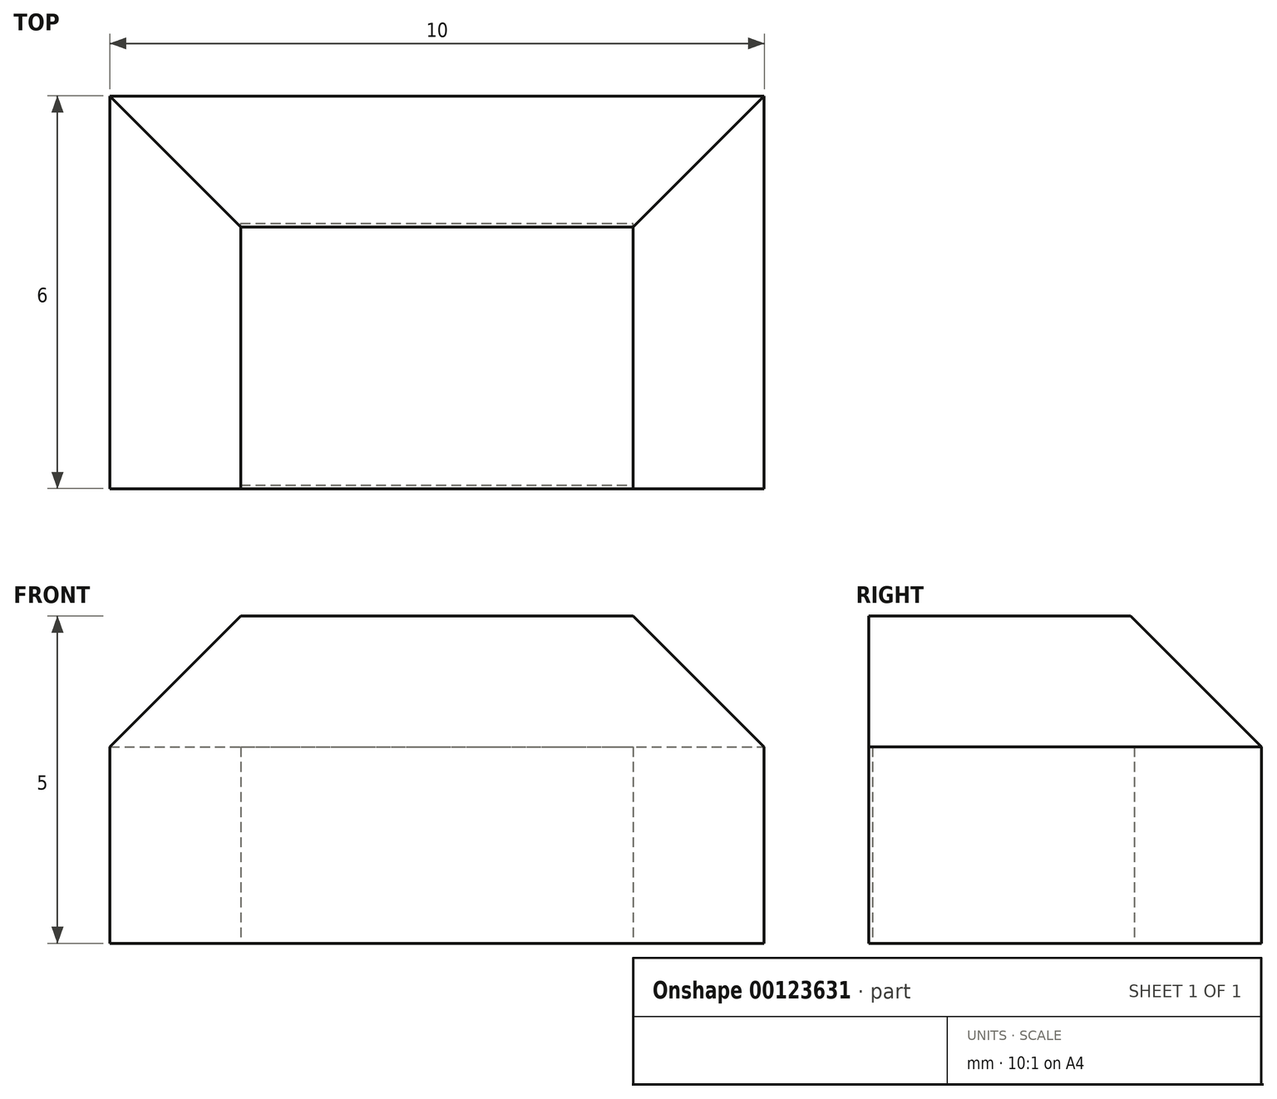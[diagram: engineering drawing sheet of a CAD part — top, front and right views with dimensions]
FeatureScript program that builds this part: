
annotation { "Feature Type Name" : "Feature", "Feature Type Description" : "" }
export const myFeature = defineFeature(function(context is Context, id is Id, definition is map)
    precondition{}
    {
        {
            var Q0;
            Q0=qCreatedBy(makeId("Top.planeOp"),FACE);
            var sketch = newSketch(context, id + "F0", { "sketchPlane" : qUnion([Q0])});
            skLineSegment(sketch, "E0.bottom", {"start": v(-27.54, 18.57) * mm, "end": v(-17.54, 18.57) * mm});
            skLineSegment(sketch, "E0.top", {"start": v(-27.54, 12.57) * mm, "end": v(-17.54, 12.57) * mm});
            skLineSegment(sketch, "E0.left", {"start": v(-27.54, 18.57) * mm, "end": v(-27.54, 12.57) * mm});
            skLineSegment(sketch, "E0.right", {"start": v(-17.54, 18.57) * mm, "end": v(-17.54, 12.57) * mm});
            skSolve(sketch);
        }
        {
            var Q0;
            Q0=makeQuery(id+"F0.imprint","IMPRINT",FACE,{"disambiguationData":[TD([[makeQuery(id+"F0.imprint","IMPRINT",EDGE,{"derivedFrom":sQuery(id+"F0.wireOp",EDGE,"E0.bottom")}),-1.0]])]});
            var sketch = newSketch(context, id + "F1", { "sketchPlane" : qUnion([Q0])});
            skLineSegment(sketch, "E1.bottom", {"start": v(-25.54, 12.62) * mm, "end": v(-19.54, 12.62) * mm});
            skLineSegment(sketch, "E1.top", {"start": v(-25.54, 16.62) * mm, "end": v(-19.54, 16.62) * mm});
            skLineSegment(sketch, "E1.left", {"start": v(-25.54, 12.62) * mm, "end": v(-25.54, 16.62) * mm});
            skLineSegment(sketch, "E1.right", {"start": v(-19.54, 12.62) * mm, "end": v(-19.54, 16.62) * mm});
            skSolve(sketch);
        }
        {
            var Q0;
            Q0=makeQuery(id+"F0.imprint","IMPRINT",FACE,{"disambiguationData":[TD([[makeQuery(id+"F0.imprint","IMPRINT",EDGE,{"derivedFrom":sQuery(id+"F0.wireOp",EDGE,"E0.bottom")}),-1.0]])]});
            extrude(context, id + "F2", {"entities" : qUnion([Q0]), "depth" : 5 * mm});
        }
        {
            var Q0;
            Q0=makeQuery(id+"F1.imprint","IMPRINT",FACE,{"disambiguationData":[TD([[makeQuery(id+"F1.imprint","IMPRINT",EDGE,{"derivedFrom":sQuery(id+"F1.wireOp",EDGE,"E1.bottom")}),1.0]])]});
            extrude(context, id + "F3", {"entities" : qUnion([Q0]), "operationType" : NewBodyOperationType.REMOVE, "depth" : 3 * mm});
        }
        {
            var Q0;
            Q0=makeQuery(id+"F2.opExtrude","CAP_EDGE",EDGE,{"disambiguationData":[OSD([sQuery(id+"F0.wireOp",EDGE,"E0.left")])],"isStart":false});
            var Q1;
            Q1=makeQuery(id+"F2.opExtrude","CAP_EDGE",EDGE,{"disambiguationData":[OSD([sQuery(id+"F0.wireOp",EDGE,"E0.bottom")])],"isStart":false});
            var Q2;
            Q2=makeQuery(id+"F2.opExtrude","CAP_EDGE",EDGE,{"disambiguationData":[OSD([sQuery(id+"F0.wireOp",EDGE,"E0.right")])],"isStart":false});
            chamfer(context, id + "F4", {"entities" : qUnion([Q0, Q1, Q2]), "width" : 2 * mm, "tangentPropagation" : true});
        }
    });
